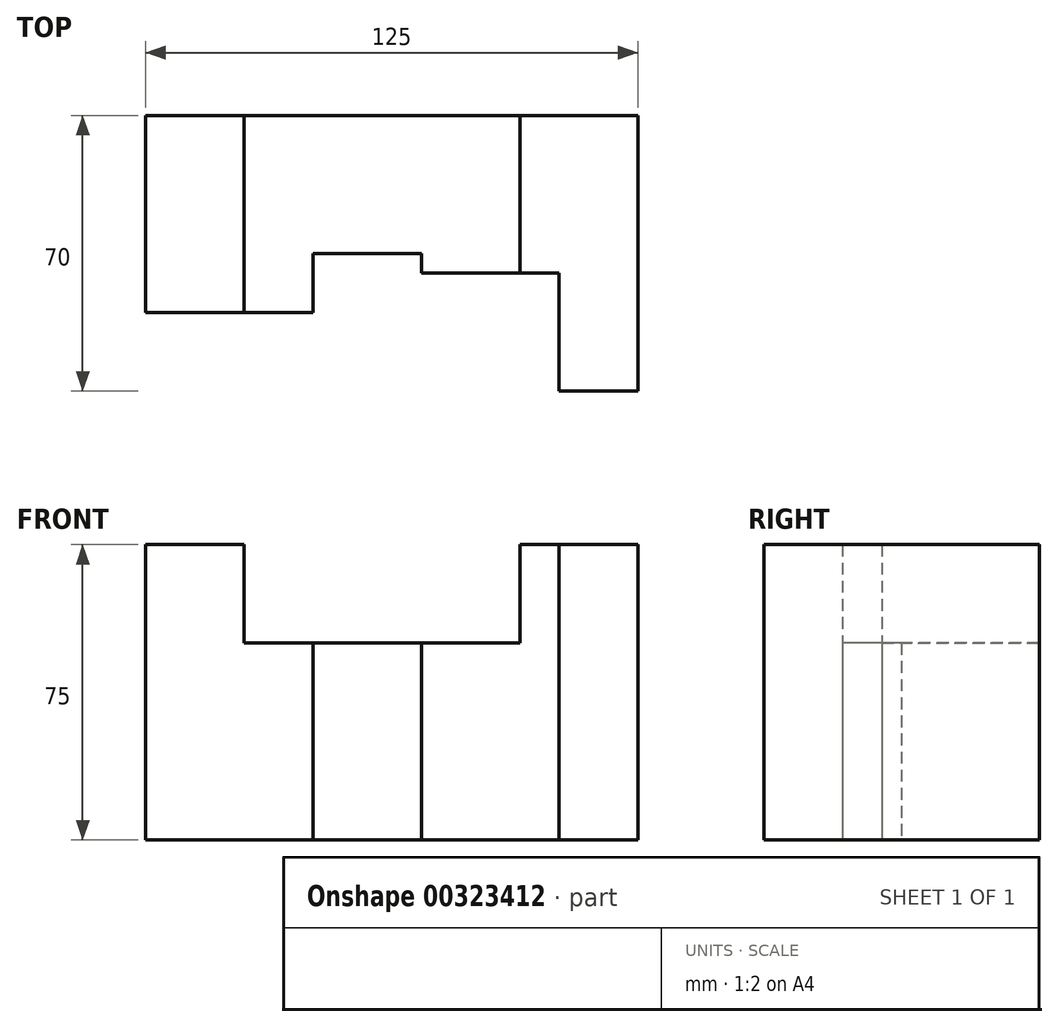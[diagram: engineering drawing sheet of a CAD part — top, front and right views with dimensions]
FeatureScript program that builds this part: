
annotation { "Feature Type Name" : "Feature", "Feature Type Description" : "" }
export const myFeature = defineFeature(function(context is Context, id is Id, definition is map)
    precondition{}
    {
        {
            var Q0;
            Q0=qCreatedBy(makeId("Top.planeOp"),FACE);
            var sketch = newSketch(context, id + "F0", { "sketchPlane" : qUnion([Q0])});
            skLineSegment(sketch, "E0", {"start": v(0, 0) * mm, "end": v(0, 50) * mm});
            skLineSegment(sketch, "E1", {"start": v(0, 50) * mm, "end": v(125, 50) * mm});
            skLineSegment(sketch, "E2", {"start": v(125, 50) * mm, "end": v(125, -20) * mm});
            skLineSegment(sketch, "E3", {"start": v(125, -20) * mm, "end": v(105, -20) * mm});
            skLineSegment(sketch, "E4", {"start": v(105, -20) * mm, "end": v(105, 10) * mm});
            skLineSegment(sketch, "E5", {"start": v(105, 10) * mm, "end": v(70, 10) * mm});
            skLineSegment(sketch, "E6", {"start": v(70, 10) * mm, "end": v(70, 15) * mm});
            skLineSegment(sketch, "E7", {"start": v(70, 15) * mm, "end": v(42.5, 15) * mm});
            skLineSegment(sketch, "E8", {"start": v(42.5, 15) * mm, "end": v(42.5, 0) * mm});
            skLineSegment(sketch, "E9", {"start": v(42.5, 0) * mm, "end": v(0, 0) * mm});
            skLineSegment(sketch, "E10", {"start": v(25, 50) * mm, "end": v(25, 0) * mm});
            skLineSegment(sketch, "E11", {"start": v(95, 10) * mm, "end": v(95, 50) * mm});
            skSolve(sketch);
        }
        {
            var Q0;
            {var subQ0=sQuery(id+"F0.wireOp",EDGE,"E0");Q0=makeQuery(id+"F0.imprint","IMPRINT",FACE,{"disambiguationData":[TD([[makeQuery(id+"F0.imprint","IMPRINT",EDGE,{"derivedFrom":subQ0}),-1.0]])]});}
            var Q1;
            {var subQ1=sQuery(id+"F0.wireOp",EDGE,"E2");Q1=makeQuery(id+"F0.imprint","IMPRINT",FACE,{"disambiguationData":[TD([[makeQuery(id+"F0.imprint","IMPRINT",EDGE,{"derivedFrom":subQ1}),-1.0]])]});}
            extrude(context, id + "F1", {"entities" : qUnion([Q0, Q1]), "depth" : (15 * 5) * mm});
        }
        {
            var Q0;
            {var subQ0=sQuery(id+"F0.wireOp",EDGE,"E6");Q0=makeQuery(id+"F0.imprint","IMPRINT",FACE,{"disambiguationData":[TD([[makeQuery(id+"F0.imprint","IMPRINT",EDGE,{"derivedFrom":subQ0}),-1.0]])]});}
            extrude(context, id + "F2", {"entities" : qUnion([Q0]), "operationType" : NewBodyOperationType.ADD, "depth" : 50 * mm});
        }
    });
